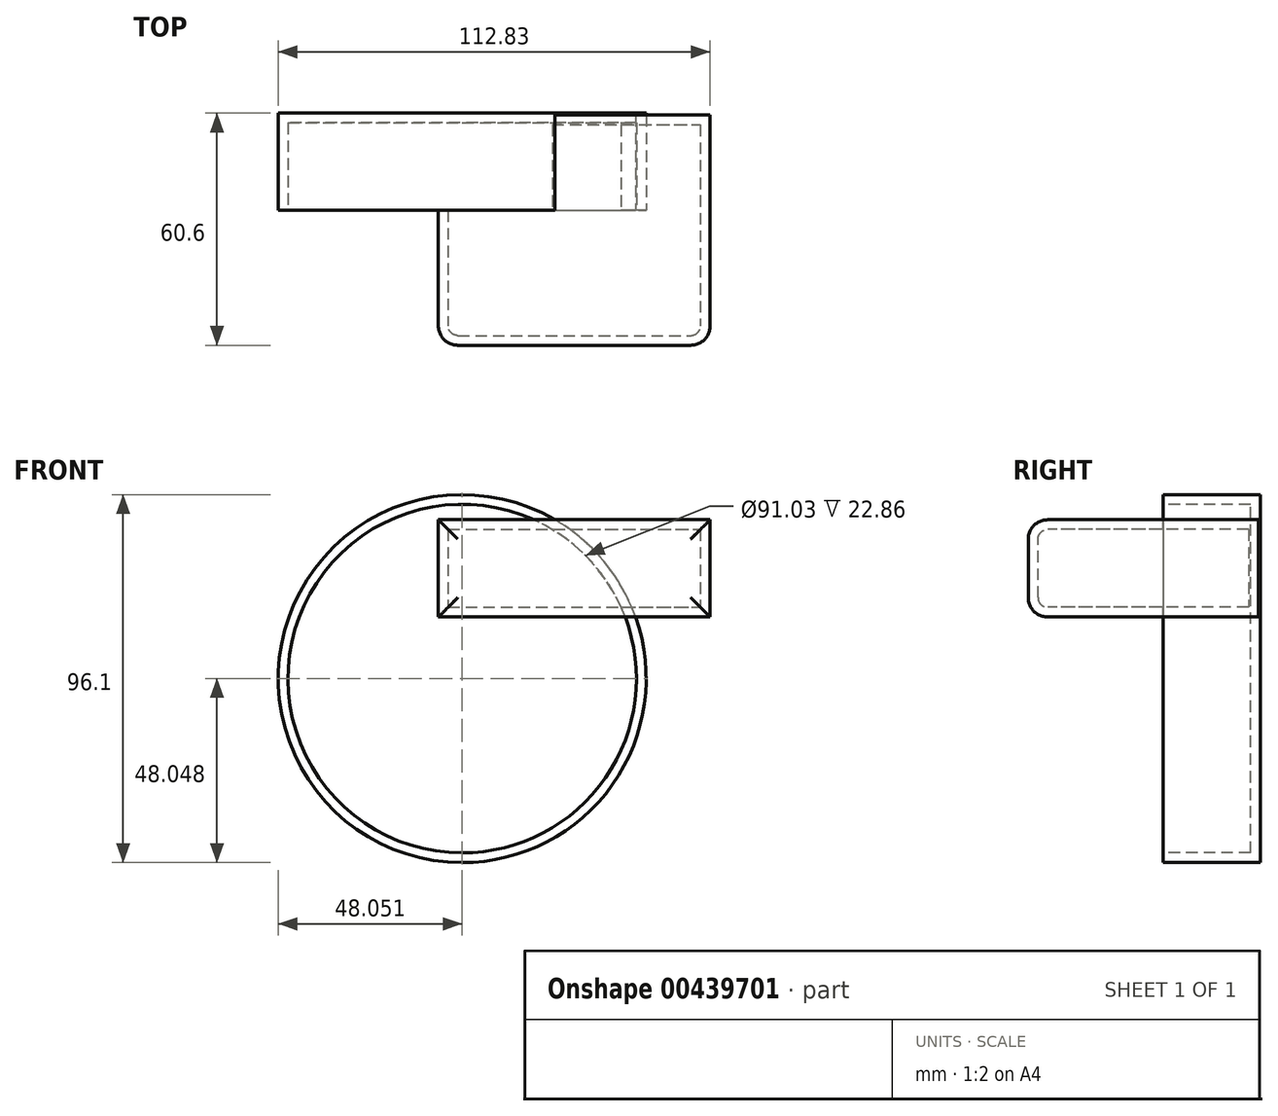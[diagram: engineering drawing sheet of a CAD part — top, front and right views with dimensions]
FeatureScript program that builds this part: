
annotation { "Feature Type Name" : "Feature", "Feature Type Description" : "" }
export const myFeature = defineFeature(function(context is Context, id is Id, definition is map)
    precondition{}
    {
        {
            var Q0;
            Q0=qCreatedBy(makeId("Top.planeOp"),FACE);
            var sketch = newSketch(context, id + "F0", { "sketchPlane" : qUnion([Q0])});
            skLineSegment(sketch, "E0.bottom", {"start": v(-50.57, 24.89) * mm, "end": v(20.43, 24.89) * mm});
            skLineSegment(sketch, "E0.top", {"start": v(-50.57, -35.2) * mm, "end": v(20.43, -35.2) * mm});
            skLineSegment(sketch, "E0.left", {"start": v(-50.57, 24.89) * mm, "end": v(-50.57, -35.2) * mm});
            skLineSegment(sketch, "E0.right", {"start": v(20.43, 24.89) * mm, "end": v(20.43, -35.2) * mm});
            skSolve(sketch);
        }
        {
            var Q0;
            Q0 = qSketchRegion(id + "F0", true);
            extrude(context, id + "F1", {"entities" : qUnion([Q0]), "depth" : 25.4 * mm});
        }
        {
            var Q0;
            Q0=qCreatedBy(makeId("Front.planeOp"),FACE);
            var sketch = newSketch(context, id + "F2", { "sketchPlane" : qUnion([Q0])});
            skCircle(sketch, "E1", {"center": v(-44.35, -16.1) * mm, "radius": 48.05 * mm});
            skSolve(sketch);
        }
        {
            var Q0;
            Q0 = qSketchRegion(id + "F2", true);
            extrude(context, id + "F3", {"entities" : qUnion([Q0]), "operationType" : NewBodyOperationType.ADD, "oppositeDirection" : true, "depth" : 25.4 * mm});
        }
        {
            var Q0;
            Q0=makeQuery(id+"F1.opExtrude","SWEPT_FACE",FACE,{"disambiguationData":[OSD([sQuery(id+"F0.wireOp",EDGE,"E0.top")])]});
            fillet(context, id + "F4", {"entities" : qUnion([Q0]), "radius" : 5.08 * mm, "tangentPropagation" : true, "allowEdgeOverflow" : false});
        }
        {
            var Q0;
            Q0=makeQuery(id+"F3.opExtrude","CAP_FACE",FACE,{"disambiguationData":[OSD([sQuery(id+"F2.wireOp",EDGE,"E1")])],"isStart":true});
            shell(context, id + "F5", {"entities" : qUnion([Q0]), "thickness" : 2.54 * mm});
        }
    });
